# Revit family: Mixer-Basin-Caroma Nordic Care-150mm1
name_source: partatom
category: Plumbing Fixtures
revit_build: Autodesk Revit 2014 (Build: 20131024_2115(x64)
units: mm (PartAtom-declared; Revit-internal decimal feet)

## types (2) — shared parameters
Assembly Code = D2020300
CW Connection = Yes
CWFU = 1.98
Connector Radius = 10 mm  [stored 0.0328084 ft]
Description = Nordic’s long life ceramic disc mixer cartridge ensures low maintenance and drip free performance. Temperature and flow settings can be pre-set, making Nordic ideal for use by small children or the elderly. The energy saving Econoflow feature delivers maximum water flow when the handle is lifted to its uppermost position.
HW Connection = Yes
HWFU = 1.98
Height_ANZRS = 183 mm
Length_ANZRS = 221 mm  [stored 0.725066 ft]
Manufacturer = GWA Bathrooms & Kitchens
Material_ANZRS = Metal-Chrome-Caroma
ModifiedIssue_ANZRS = 20150508 $
URL = http://specify.caroma.com.au
Vent Connection = No
WELSRating_ANZRS = WELS 4 star rated, 7.5L/min
Waste Connection = No
Width_ANZRS = 59 mm
zero-valued in all types: Cost, Default Elevation

## per-type parameters (varying)
| type | Model | Type Comments | Warm |
| Warm/Cold | 90967C4A | Caroma Nordic Plus Care Sink Mixer (150mm) - Warm/Cold | Yes |
| Hot/Cold | 90966C4A | Caroma Nordic Plus Care Sink Mixer (150mm) - Hot/Cold | No |

note: [stored X ft] marks values corroborated as IEEE doubles in the binary element streams (Revit-internal decimal feet)

## geometry (parser evidence)
native form markers: Blend x10, Sweep x1
no freeform markers — native parametric forms only
